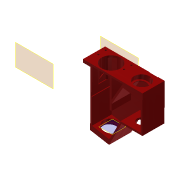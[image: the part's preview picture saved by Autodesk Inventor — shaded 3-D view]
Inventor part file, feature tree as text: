
AUTODESK INVENTOR PART (.ipt)
format: ipt  version: 2022 (Build 260153000, 153)  size: 415,744 bytes
history: native  units: mm
features: other x16, sketch x15, reference x15, extrude x13, plane x6, projected_geometry x6, hole x2, pattern_linear x1
ambient origin geometry x8: Origin, YZ Plane, XZ Plane, XY Plane, X Axis, Y Axis, Z Axis, Center Point
bodies: Solid1 (feature_tree)
feature tree (74):
  plane  "Work Plane1"
  plane  "Work Plane2"
  extrude  "Extrusion1"  TaperAngle=180.0deg  [1 undecoded]
  extrude  "Extrusion2"  Depth=3.0mm TaperAngle=0.0deg
  plane  "Work Plane3"
  plane  "Work Plane4"
  extrude  "Extrusion5"  Depth=3.0mm
  plane  "Work Plane5"
  extrude  "Extrusion9"  Depth=30.7mm
  plane  "Arbeitsebene11"
  extrude  "Extrusion17"  Depth=15.0mm TaperAngle=0.0deg
  extrude  "Extrusion18"  Depth=2.0mm
  hole  "Bohrung4"  [1 undecoded]
  pattern_linear  "Rechteckige Anordnung1"  Count1=6  [1 undecoded]
  extrude  "Extrusion21"  Depth=6.0mm
  extrude  "Extrusion23"  Depth=3.0mm
  hole  "Bohrung5"  [1 undecoded]
  extrude  "Extrusion24"  Depth=3.0mm
  extrude  "Extrusion25"  Depth=28.0mm
  extrude  "Extrusion26"  Depth=6.0mm TaperAngle=0.0deg
  extrude  "Extrusion27"  Depth=6.0mm
  extrude  "Extrusion28"  Depth=6.0mm
  sketch  "Sketch2"  dims[d0=4.0mm d1=180.0deg]
  sketch  "Sketch3"  dims[d2=3.0mm d6=4.0mm d7=0.0mm d8=3.0mm d14=32.0mm d15=0.0mm]
  sketch  "Sketch7"  dims[d23=3.0mm d33=24.0mm]
  sketch  "Sketch11"  dims[d34=5.0mm d35=0.0mm d43=30.7mm]
  sketch  "Sketch21"  dims[d44=60.0mm d45=0.0mm d101=15.0mm d102=0.0mm]
  sketch  "Sketch22"  dims[d104=2.0mm d105=0.0mm d110=8.0mm]
  projected_geometry  "Projected Loop10"
  sketch  "Skizze26"  dims[d124=2.8mm d125=6.0mm d126=4.0mm d127=2.0mm d128=90.0deg d129=12.0mm d130=20.594885mm d131=120.0mm d133=12.5mm]
  reference  "Referenz23"
  reference  "Referenz24"
  reference  "Referenz25"
  reference  "Referenz26"
  sketch  "Skizze28"  dims[d134=1.0mm]
  reference  "Referenz27"
  reference  "Referenz28"
  projected_geometry  "Projizierte Kontur12"
  reference  "Referenz32"
  reference  "Referenz33"
  reference  "Referenz34"
  reference  "Referenz35"
  reference  "Referenz36"
  sketch  "Skizze30"  dims[d135=1.0mm]
  sketch  "Skizze31"  dims[d136=0.5mm d137=0.0mm]
  projected_geometry  "Projizierte Kontur13"
  sketch  "Skizze32"  dims[d156=3.0mm]
  projected_geometry  "Projizierte Kontur14"
  sketch  "Skizze34"  dims[d157=3.0mm]
  projected_geometry  "Projizierte Kontur16"
  sketch  "Skizze35"  dims[d158=1.0mm]
  reference  "Referenz40"
  sketch  "Skizze36"  dims[d159=94.0mm]
  reference  "Referenz41"
  reference  "Referenz42"
  sketch  "Skizze37"  dims[d160=85.0mm d161=60.0mm d163=34.0mm d165=3.0mm d166=3.0mm d167=3.0mm d168=28.0mm d169=5.0mm d170=0.0mm d171=25.5mm d172=5.0mm d173=3.0mm d174=6.0mm d175=8.0mm d176=5.0mm d177=90.0deg d178=8.0mm d179=20.594885mm d180=12.0mm d181=5.0mm d182=2.8mm d183=2.8mm d185=2.8mm d186=2.8mm d187=12.0mm d188=12.0mm d189=0.0mm d190=42.0mm d191=0.0mm d192=0.0mm d193=20.0mm d194=0.0mm d202=10.0mm d203=0.0mm d204=25.4mm d205=20.0mm d206=1.0mm d207=0.0mm d208=25.4mm d209=1.0mm d210=0.0mm d211=10.0mm d213=1.0mm d214=15.0mm d215=30.0mm d216=6.0mm d217=15.0mm d218=0.0mm]
  projected_geometry  "Projizierte Kontur17"
  reference  "Referenz43"
  other  "<userpath>\Downloads\cellSTORM\cellSTORM_v5_microsocpe.iam"
  other  "cellSTORM_v5_microsocpe.iam"
  other  "30_Cube_Z_Focus_MGN_NEMA_rail:1"
  other  "00_MGN12H, LINEAR GUIDE BLOCK:1"
  other  "<userpath>\Documents\GitHub\cellstorm\INVENTOR\cellSTORM_v5_microsocpe.iam"
  other  "PF10-03-P01-Step:3"
  other  "30_Cube_Z_Focus_MGN12_NEMA_slide_part2:1"
  other  "PF10-03-P01-Step:4"
  other  "00_Eyepiece_20x_WF:1"
  other  "cellSTORM_lightpath:2"
  other  "<userpath>\Documents\GitHub\cellstorm\INVENTOR\cellSTORM_v6.iam"
  other  "cellSTORM_v6.iam"
  other  "00_Arduino_CNC_Assembly:1"
  other  "Arduino_Uno_CNC_Shield_V3_2"
  other  "cellSTORM_v5.iam"
  other  "cellSTORM_v5_cellphonestage:1"
note: 4 required parameter values undecoded (feature->parameter linkage not recoverable at this tier; creation-order binding heuristic only, values carry confidence <= 0.55)
